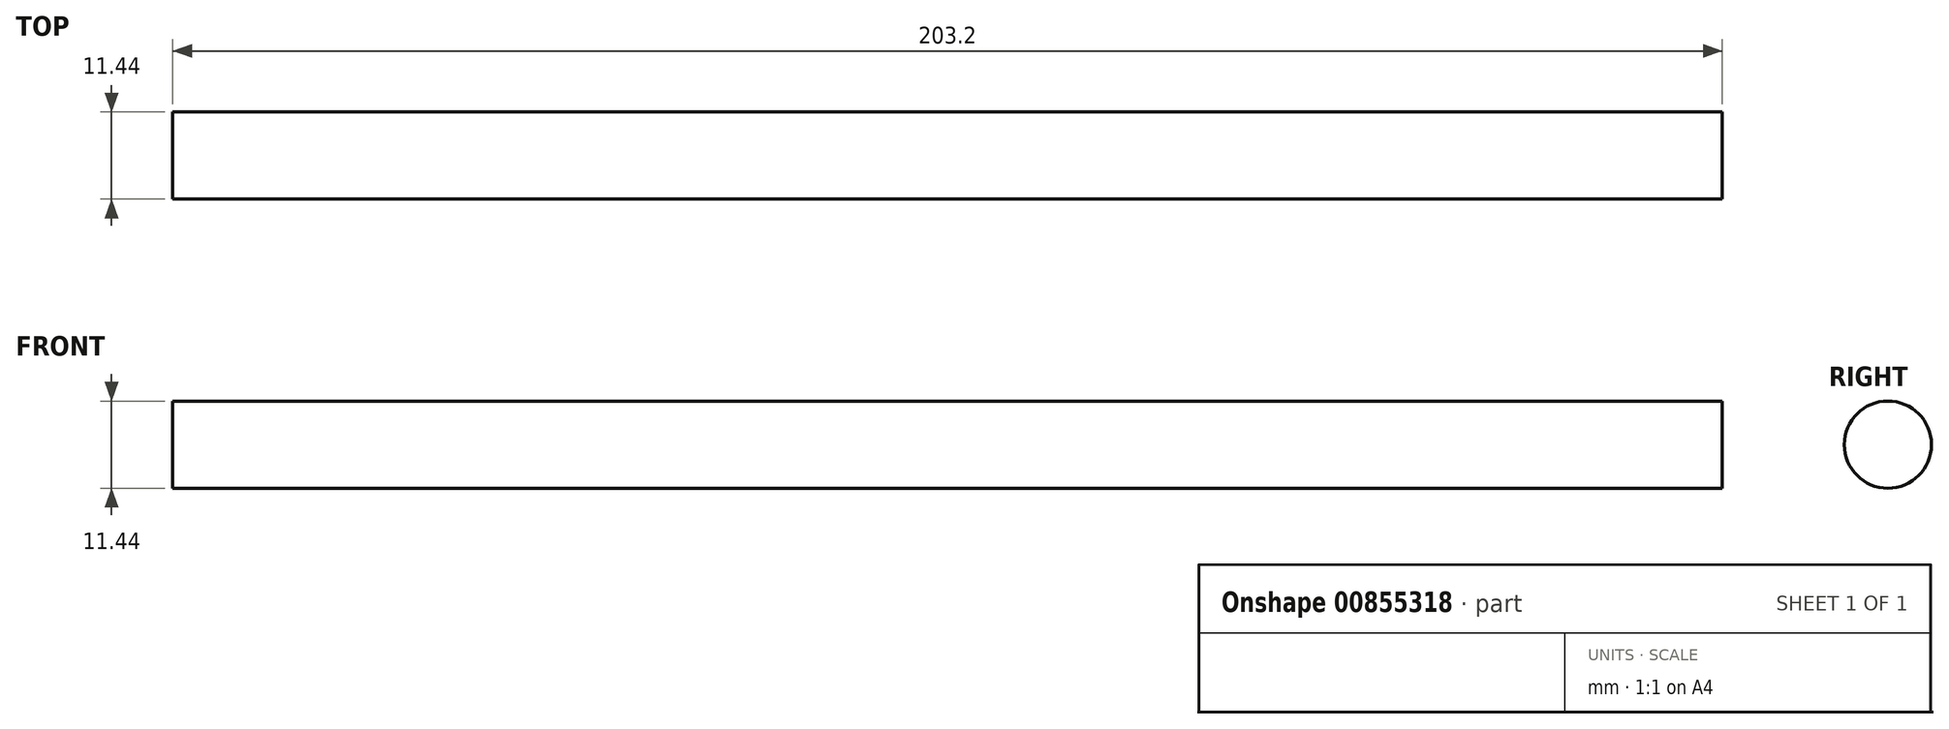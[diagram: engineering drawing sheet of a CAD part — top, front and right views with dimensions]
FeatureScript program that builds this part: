
annotation { "Feature Type Name" : "Feature", "Feature Type Description" : "" }
export const myFeature = defineFeature(function(context is Context, id is Id, definition is map)
    precondition{}
    {
        {
            var Q0;
            Q0=qCreatedBy(makeId("Right.planeOp"),FACE);
            var sketch = newSketch(context, id + "F0", { "sketchPlane" : qUnion([Q0])});
            skCircle(sketch, "E0", {"center": v(0, 0) * mm, "radius": 5.72 * mm});
            skSolve(sketch);
        }
        {
            var Q0;
            Q0=makeQuery(id+"F0.imprint","IMPRINT",FACE,{"disambiguationData":[TD([[makeQuery(id+"F0.imprint","IMPRINT",EDGE,{"derivedFrom":sQuery(id+"F0.wireOp",EDGE,"E0")}),1.0]])]});
            extrude(context, id + "F1", {"entities" : qUnion([Q0]), "depth" : 101.6 * mm, "offsetDistance" : 25.4 * mm, "hasSecondDirection" : true, "secondDirectionOppositeDirection" : true, "secondDirectionDepth" : 101.6 * mm});
        }
    });
